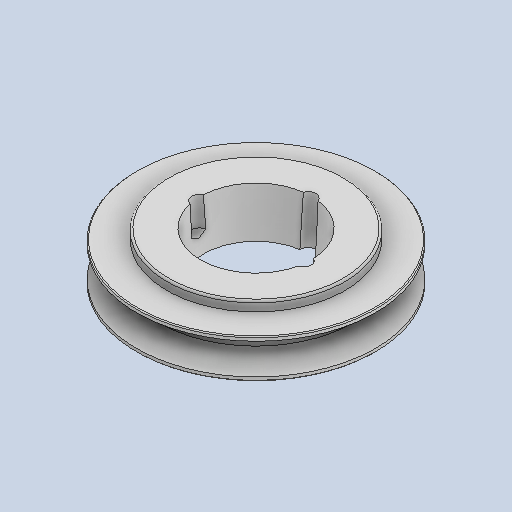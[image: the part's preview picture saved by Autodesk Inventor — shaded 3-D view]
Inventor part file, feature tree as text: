
AUTODESK INVENTOR PART (.ipt)
format: ipt  version: 2025 (Build 290162010, 162A)  size: 336,384 bytes
history: native  units: mm
features: sketch x3, fillet x2, hole x2, revolve x1
ambient origin geometry x8: Origin, YZ Plane, XZ Plane, XY Plane, X Axis, Y Axis, Z Axis, Center Point
bodies: Solid1 (feature_tree)
feature tree (8):
  revolve  "Revolution1"  [1 undecoded]
  fillet  "Fillet1"  [1 undecoded]
  fillet  "Fillet2"  Radius=1.0mm
  hole  "Hole1"  [1 undecoded]
  hole  "Hole2"  [1 undecoded]
  sketch  "Sketch1"  dims[d4=5.0mm d5=2.0mm d10=90.0deg d11=1.0mm]
  sketch  "Sketch5"  dims[d12=0.5mm d24=28.535mm]
  sketch  "Sketch6"  dims[d26=5.0mm d27=17.465mm d29=26.985mm d30=61.75mm d31=25.0mm d32=50.0mm d33=8.0mm d34=6.0mm d35=4.0mm d36=2.0mm d37=90.0deg d38=15.0mm d39=20.594885mm d40=14.835299mm d41=14.835299mm d42=8.0mm d43=6.0mm d44=4.0mm d45=2.0mm d46=90.0deg d47=15.0mm d48=20.594885mm]
note: 4 required parameter values undecoded (feature->parameter linkage not recoverable at this tier; creation-order binding heuristic only, values carry confidence <= 0.55)